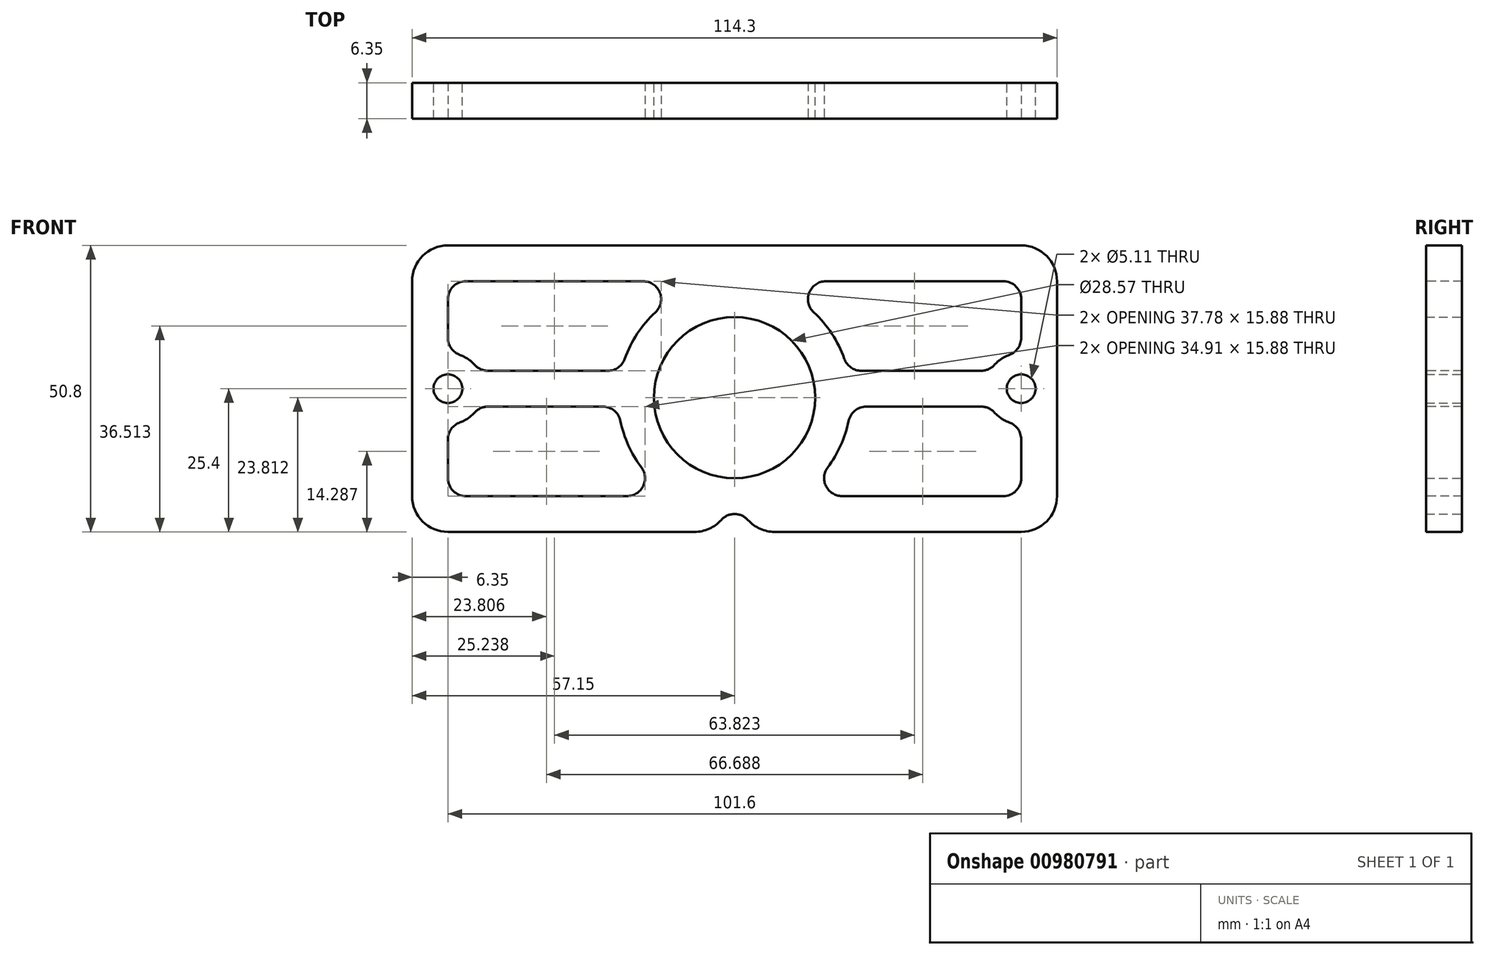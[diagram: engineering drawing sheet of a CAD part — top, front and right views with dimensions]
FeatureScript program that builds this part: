
annotation { "Feature Type Name" : "Feature", "Feature Type Description" : "" }
export const myFeature = defineFeature(function(context is Context, id is Id, definition is map)
    precondition{}
    {
        {
            var Q0;
            Q0=qCreatedBy(makeId("Front.planeOp"),FACE);
            var sketch = newSketch(context, id + "F0", { "sketchPlane" : qUnion([Q0])});
            skCircle(sketch, "E0", {"center": v(-62.07, 61.28) * mm, "radius": 32 * mm, "construction": true});
            skCircle(sketch, "E1", {"center": v(62.07, 61.28) * mm, "radius": 32 * mm, "construction": true});
            skLineSegment(sketch, "E2", {"start": v(0, 0) * mm, "end": v(0, 61.28) * mm, "construction": true});
            skLineSegment(sketch, "E3", {"start": v(-62.07, 61.28) * mm, "end": v(62.07, 61.28) * mm, "construction": true});
            skLineSegment(sketch, "E4.bottom", {"start": v(-127, 25.4) * mm, "end": v(127, 25.4) * mm, "construction": true});
            skLineSegment(sketch, "E4.top", {"start": v(-127, -25.4) * mm, "end": v(127, -25.4) * mm, "construction": true});
            skLineSegment(sketch, "E4.left", {"start": v(-127, 25.4) * mm, "end": v(-127, -25.4) * mm, "construction": true});
            skLineSegment(sketch, "E4.right", {"start": v(127, 25.4) * mm, "end": v(127, -25.4) * mm, "construction": true});
            skPoint(sketch, "E4.middle", {"position": v(0, 0) * mm});
            skCircle(sketch, "E5", {"center": v(-62.07, 61.28) * mm, "radius": 8.9 * mm, "construction": true});
            skCircle(sketch, "E6", {"center": v(62.07, 61.28) * mm, "radius": 8.9 * mm, "construction": true});
            skCircle(sketch, "E7", {"center": v(0, -1.59) * mm, "radius": 50.8 * mm, "construction": true});
            skCircle(sketch, "E8", {"center": v(-62.07, 61.28) * mm, "radius": 9.55 * mm, "construction": true});
            skCircle(sketch, "E9", {"center": v(62.07, 61.28) * mm, "radius": 9.55 * mm, "construction": true});
            skCircle(sketch, "E10", {"center": v(0, 65.72) * mm, "radius": 14.29 * mm, "construction": true});
            skCircle(sketch, "E11", {"center": v(0, -1.59) * mm, "radius": 14.29 * mm});
            skCircle(sketch, "E12", {"center": v(-114.3, 12.7) * mm, "radius": 2.55 * mm, "construction": true});
            skCircle(sketch, "E13.0.1.0", {"center": v(-114.3, -12.7) * mm, "radius": 2.55 * mm, "construction": true});
            skCircle(sketch, "E13.1.0.0", {"center": v(-88.9, 12.7) * mm, "radius": 2.55 * mm, "construction": true});
            skCircle(sketch, "E13.1.1.0", {"center": v(-88.9, -12.7) * mm, "radius": 2.55 * mm, "construction": true});
            skCircle(sketch, "E13.2.0.0", {"center": v(-63.5, 12.7) * mm, "radius": 2.55 * mm, "construction": true});
            skCircle(sketch, "E13.2.1.0", {"center": v(-63.5, -12.7) * mm, "radius": 2.55 * mm, "construction": true});
            skCircle(sketch, "E13.3.0.0", {"center": v(-38.1, 12.7) * mm, "radius": 2.55 * mm, "construction": true});
            skCircle(sketch, "E13.3.1.0", {"center": v(-38.1, -12.7) * mm, "radius": 2.55 * mm, "construction": true});
            skCircle(sketch, "E13.4.0.0", {"center": v(-12.7, 12.7) * mm, "radius": 2.55 * mm, "construction": true});
            skCircle(sketch, "E13.4.1.0", {"center": v(-12.7, -12.7) * mm, "radius": 2.55 * mm, "construction": true});
            skCircle(sketch, "E13.5.0.0", {"center": v(12.7, 12.7) * mm, "radius": 2.55 * mm, "construction": true});
            skCircle(sketch, "E13.5.1.0", {"center": v(12.7, -12.7) * mm, "radius": 2.55 * mm, "construction": true});
            skCircle(sketch, "E13.6.0.0", {"center": v(38.1, 12.7) * mm, "radius": 2.55 * mm, "construction": true});
            skCircle(sketch, "E13.6.1.0", {"center": v(38.1, -12.7) * mm, "radius": 2.55 * mm, "construction": true});
            skCircle(sketch, "E13.7.0.0", {"center": v(63.5, 12.7) * mm, "radius": 2.55 * mm, "construction": true});
            skCircle(sketch, "E13.7.1.0", {"center": v(63.5, -12.7) * mm, "radius": 2.55 * mm, "construction": true});
            skCircle(sketch, "E13.8.0.0", {"center": v(88.9, 12.7) * mm, "radius": 2.55 * mm, "construction": true});
            skCircle(sketch, "E13.8.1.0", {"center": v(88.9, -12.7) * mm, "radius": 2.55 * mm, "construction": true});
            skCircle(sketch, "E13.9.0.0", {"center": v(114.3, 12.7) * mm, "radius": 2.55 * mm, "construction": true});
            skCircle(sketch, "E13.9.1.0", {"center": v(114.3, -12.7) * mm, "radius": 2.55 * mm, "construction": true});
            skLineSegment(sketch, "E13.direction1", {"start": v(-114.3, 12.7) * mm, "end": v(-88.9, 12.7) * mm, "construction": true});
            skLineSegment(sketch, "E13.direction2", {"start": v(-114.3, 12.7) * mm, "end": v(-114.3, -12.7) * mm, "construction": true});
            skCircle(sketch, "E14", {"center": v(-50.8, 0) * mm, "radius": 2.55 * mm});
            skCircle(sketch, "E15", {"center": v(50.8, 0) * mm, "radius": 2.55 * mm});
            skCircle(sketch, "E16", {"center": v(-50.8, 0) * mm, "radius": 6.35 * mm, "construction": true});
            skCircle(sketch, "E17", {"center": v(50.8, 0) * mm, "radius": 6.35 * mm, "construction": true});
            skLineSegment(sketch, "E18", {"start": v(-74.77, 39.28) * mm, "end": v(-62.07, 61.28) * mm, "construction": true});
            skLineSegment(sketch, "E19", {"start": v(-62.07, 61.28) * mm, "end": v(-49.37, 83.27) * mm, "construction": true});
            skCircle(sketch, "E20", {"center": v(-74.77, 39.28) * mm, "radius": 2.55 * mm, "construction": true});
            skCircle(sketch, "E21", {"center": v(-49.37, 83.27) * mm, "radius": 2.55 * mm, "construction": true});
            skLineSegment(sketch, "E22.MirrorCS", {"start": v(74.77, 39.28) * mm, "end": v(62.07, 61.28) * mm, "construction": true});
            skCircle(sketch, "E23.MirrorC", {"center": v(74.77, 39.28) * mm, "radius": 2.55 * mm, "construction": true});
            skLineSegment(sketch, "E24.MirrorCS", {"start": v(62.07, 61.28) * mm, "end": v(49.37, 83.27) * mm, "construction": true});
            skCircle(sketch, "E25.MirrorC", {"center": v(49.37, 83.27) * mm, "radius": 2.55 * mm, "construction": true});
            skCircle(sketch, "E26", {"center": v(0, 65.72) * mm, "radius": 53.34 * mm, "construction": true});
            skCircle(sketch, "E27", {"center": v(0, 65.72) * mm, "radius": 25.4 * mm, "construction": true});
            skCircle(sketch, "E28", {"center": v(0, -1.59) * mm, "radius": 20.64 * mm, "construction": true});
            skCircle(sketch, "E29", {"center": v(0, 65.72) * mm, "radius": 55.88 * mm, "construction": true});
            skCircle(sketch, "E30", {"center": v(0, 91.12) * mm, "radius": 2.55 * mm, "construction": true});
            skCircle(sketch, "E31", {"center": v(0, 40.32) * mm, "radius": 2.55 * mm, "construction": true});
            skLineSegment(sketch, "E32", {"start": v(0, 40.32) * mm, "end": v(0, 65.72) * mm, "construction": true});
            skLineSegment(sketch, "E33", {"start": v(0, 65.72) * mm, "end": v(0, 91.12) * mm, "construction": true});
            skCircle(sketch, "E34", {"center": v(0, -1.59) * mm, "radius": 41.91 * mm, "construction": true});
            skCircle(sketch, "E35", {"center": v(0, -1.59) * mm, "radius": 44.45 * mm, "construction": true});
            skCircle(sketch, "E36", {"center": v(0, 65.72) * mm, "radius": 28.58 * mm, "construction": true});
            skArc(sketch, "E37", {"start": v(30.1, 62.76) * mm, "mid": v(0, 94.3) * mm, "end": v(-30.1, 62.76) * mm});
            skLineSegment(sketch, "E38.bottom", {"start": v(-57.15, 25.4) * mm, "end": v(57.15, 25.4) * mm});
            skLineSegment(sketch, "E38.top", {"start": v(-57.15, -25.4) * mm, "end": v(57.15, -25.4) * mm, "construction": true});
            skLineSegment(sketch, "E38.left", {"start": v(-57.15, 25.4) * mm, "end": v(-57.15, -25.4) * mm});
            skLineSegment(sketch, "E38.right", {"start": v(57.15, 25.4) * mm, "end": v(57.15, -25.4) * mm});
            skArc(sketch, "E39", {"start": v(3.18, -25.4) * mm, "mid": v(0, -22.22) * mm, "end": v(-3.18, -25.4) * mm});
            skLineSegment(sketch, "E40", {"start": v(-3.18, -25.4) * mm, "end": v(-57.15, -25.4) * mm});
            skLineSegment(sketch, "E41", {"start": v(3.18, -25.4) * mm, "end": v(57.15, -25.4) * mm});
            skSolve(sketch);
        }
        {
            var Q0;
            Q0=qSketchRegion(id+"F0",true);
            extrude(context, id + "F1", {"entities" : qUnion([Q0]), "depth" : 6.35 * mm, "offsetDistance" : 25.4 * mm});
        }
        {
            var Q0;
            Q0=makeQuery(id+"F1.opExtrude","SWEPT_EDGE",EDGE,{"disambiguationData":[OSD([sQuery(id+"F0.wireOp",EDGE,"E38.bottom"),sQuery(id+"F0.wireOp",EDGE,"E38.left")])]});
            var Q1;
            Q1=makeQuery(id+"F1.opExtrude","SWEPT_EDGE",EDGE,{"disambiguationData":[OSD([sQuery(id+"F0.wireOp",EDGE,"E38.top"),sQuery(id+"F0.wireOp",EDGE,"E38.left")])]});
            var Q2;
            Q2=makeQuery(id+"F1.opExtrude","SWEPT_EDGE",EDGE,{"disambiguationData":[OSD([sQuery(id+"F0.wireOp",EDGE,"E38.top"),sQuery(id+"F0.wireOp",EDGE,"E38.right")])]});
            var Q3;
            Q3=makeQuery(id+"F1.opExtrude","SWEPT_EDGE",EDGE,{"disambiguationData":[OSD([sQuery(id+"F0.wireOp",EDGE,"E38.bottom"),sQuery(id+"F0.wireOp",EDGE,"E38.right")])]});
            var Q4;
            Q4=makeQuery(id+"F1.opExtrude","SWEPT_EDGE",EDGE,{"disambiguationData":[OSD([sQuery(id+"F0.wireOp",EDGE,"E39"),sQuery(id+"F0.wireOp",EDGE,"E40")])]});
            var Q5;
            Q5=makeQuery(id+"F1.opExtrude","SWEPT_EDGE",EDGE,{"disambiguationData":[OSD([sQuery(id+"F0.wireOp",EDGE,"E39"),sQuery(id+"F0.wireOp",EDGE,"E41")])]});
            fillet(context, id + "F2", {"entities" : qUnion([Q0, Q1, Q2, Q3, Q4, Q5]), "radius" : 6.35 * mm, "tangentPropagation" : true, "allowEdgeOverflow" : false});
        }
        {
            var Q0;
            Q0=makeQuery(id+"F1.opExtrude","CAP_FACE",FACE,{"disambiguationData":[OSD([sQuery(id+"F0.wireOp",EDGE,"E11"),sQuery(id+"F0.wireOp",EDGE,"E14"),sQuery(id+"F0.wireOp",EDGE,"E15"),sQuery(id+"F0.wireOp",EDGE,"E38.bottom"),sQuery(id+"F0.wireOp",EDGE,"E38.left"),sQuery(id+"F0.wireOp",EDGE,"E38.right"),sQuery(id+"F0.wireOp",EDGE,"E39"),sQuery(id+"F0.wireOp",EDGE,"E40"),sQuery(id+"F0.wireOp",EDGE,"E41")])],"isStart":false});
            var sketch = newSketch(context, id + "F3", { "sketchPlane" : qUnion([Q0])});
            skLineSegment(sketch, "E42.0", {"start": v(-50.8, 19.05) * mm, "end": v(-50.8, -19.05) * mm, "construction": true});
            skLineSegment(sketch, "E42.1", {"start": v(50.8, 19.05) * mm, "end": v(50.8, -19.05) * mm, "construction": true});
            skLineSegment(sketch, "E42.2", {"start": v(7.1, -19.05) * mm, "end": v(50.8, -19.05) * mm, "construction": true});
            skLineSegment(sketch, "E42.3", {"start": v(-50.8, 19.05) * mm, "end": v(50.8, 19.05) * mm, "construction": true});
            skArc(sketch, "E42.4", {"start": v(7.1, -19.05) * mm, "mid": v(0, -15.88) * mm, "end": v(-7.1, -19.05) * mm, "construction": true});
            skLineSegment(sketch, "E42.5", {"start": v(-7.1, -19.05) * mm, "end": v(-50.8, -19.05) * mm, "construction": true});
            skCircle(sketch, "E43", {"center": v(-50.8, 0) * mm, "radius": 6.35 * mm, "construction": true});
            skCircle(sketch, "E44", {"center": v(0, -1.59) * mm, "radius": 20.64 * mm, "construction": true});
            skCircle(sketch, "E45", {"center": v(50.8, 0) * mm, "radius": 6.35 * mm, "construction": true});
            skLineSegment(sketch, "E46", {"start": v(-43.7, 3.18) * mm, "end": v(-22.45, 3.18) * mm});
            skLineSegment(sketch, "E47", {"start": v(-43.7, -3.18) * mm, "end": v(-23.33, -3.18) * mm});
            skLineSegment(sketch, "E48", {"start": v(-50.8, 8.98) * mm, "end": v(-50.8, 15.87) * mm});
            skLineSegment(sketch, "E49", {"start": v(-47.63, 19.05) * mm, "end": v(-16.19, 19.05) * mm});
            skArc(sketch, "E50", {"start": v(-46.07, 4.23) * mm, "mid": v(-47.26, 5.27) * mm, "end": v(-48.68, 5.99) * mm});
            skArc(sketch, "E51", {"start": v(-14.03, 13.55) * mm, "mid": v(-17.25, 9.75) * mm, "end": v(-19.46, 5.3) * mm});
            skPoint(sketch, "E52.visualSharp", {"position": v(-50.8, 19.05) * mm});
            skArc(sketch, "E52.filletArc", {"start": v(-47.63, 19.05) * mm, "mid": v(-49.87, 18.12) * mm, "end": v(-50.8, 15.87) * mm});
            skPoint(sketch, "E53.visualSharp", {"position": v(-50.8, 6.35) * mm});
            skArc(sketch, "E53.filletArc", {"start": v(-50.8, 8.98) * mm, "mid": v(-50.22, 7.15) * mm, "end": v(-48.68, 5.99) * mm});
            skPoint(sketch, "E54.visualSharp", {"position": v(-45.3, 3.18) * mm});
            skArc(sketch, "E54.filletArc", {"start": v(-46.07, 4.23) * mm, "mid": v(-45, 3.45) * mm, "end": v(-43.7, 3.18) * mm});
            skPoint(sketch, "E55.visualSharp", {"position": v(-20.08, 3.17) * mm});
            skArc(sketch, "E55.filletArc", {"start": v(-22.45, 3.18) * mm, "mid": v(-20.62, 3.76) * mm, "end": v(-19.46, 5.3) * mm});
            skPoint(sketch, "E56.visualSharp", {"position": v(0, 19.05) * mm});
            skArc(sketch, "E56.filletArc", {"start": v(-14.03, 13.55) * mm, "mid": v(-13.23, 17.03) * mm, "end": v(-16.19, 19.05) * mm});
            skLineSegment(sketch, "E57", {"start": v(-50.8, 0) * mm, "end": v(50.8, 0) * mm, "construction": true});
            skLineSegment(sketch, "E58", {"start": v(0, -25.4) * mm, "end": v(0, 19.05) * mm, "construction": true});
            skArc(sketch, "E59.MirrorCS", {"start": v(46.07, 4.23) * mm, "mid": v(47.26, 5.27) * mm, "end": v(48.68, 5.99) * mm});
            skArc(sketch, "E60.MirrorCS", {"start": v(46.07, 4.23) * mm, "mid": v(45, 3.45) * mm, "end": v(43.7, 3.18) * mm});
            skArc(sketch, "E61.MirrorCS", {"start": v(50.8, 8.98) * mm, "mid": v(50.22, 7.15) * mm, "end": v(48.68, 5.99) * mm});
            skArc(sketch, "E62.MirrorCS", {"start": v(47.63, 19.05) * mm, "mid": v(49.87, 18.12) * mm, "end": v(50.8, 15.87) * mm});
            skArc(sketch, "E63.MirrorCS", {"start": v(22.45, 3.18) * mm, "mid": v(20.62, 3.76) * mm, "end": v(19.46, 5.3) * mm});
            skArc(sketch, "E64.MirrorCS", {"start": v(14.03, 13.55) * mm, "mid": v(13.23, 17.03) * mm, "end": v(16.19, 19.05) * mm});
            skPoint(sketch, "E65.MirrorP", {"position": v(50.8, 19.05) * mm});
            skArc(sketch, "E66.MirrorCS", {"start": v(14.03, 13.55) * mm, "mid": v(17.25, 9.75) * mm, "end": v(19.46, 5.3) * mm});
            skPoint(sketch, "E67.MirrorP", {"position": v(50.8, 6.35) * mm});
            skLineSegment(sketch, "E68.MirrorCS", {"start": v(43.7, 3.18) * mm, "end": v(22.45, 3.18) * mm});
            skLineSegment(sketch, "E69.MirrorCS", {"start": v(50.8, 8.98) * mm, "end": v(50.8, 15.87) * mm});
            skPoint(sketch, "E70.MirrorP", {"position": v(45.3, 3.18) * mm});
            skLineSegment(sketch, "E71.MirrorCS", {"start": v(47.63, 19.05) * mm, "end": v(16.19, 19.05) * mm});
            skPoint(sketch, "E72.MirrorP", {"position": v(20.08, 3.17) * mm});
            skLineSegment(sketch, "E73", {"start": v(-50.8, -8.98) * mm, "end": v(-50.8, -15.88) * mm});
            skLineSegment(sketch, "E74", {"start": v(-47.63, -19.05) * mm, "end": v(-19.05, -19.05) * mm});
            skArc(sketch, "E75", {"start": v(-20.22, -5.71) * mm, "mid": v(-18.82, -10.05) * mm, "end": v(-16.5, -13.97) * mm});
            skArc(sketch, "E76", {"start": v(-48.68, -5.99) * mm, "mid": v(-47.26, -5.27) * mm, "end": v(-46.07, -4.23) * mm});
            skPoint(sketch, "E77.visualSharp", {"position": v(-50.8, -6.35) * mm});
            skArc(sketch, "E77.filletArc", {"start": v(-48.68, -5.99) * mm, "mid": v(-50.22, -7.15) * mm, "end": v(-50.8, -8.98) * mm});
            skPoint(sketch, "E78.visualSharp", {"position": v(-45.3, -3.18) * mm});
            skArc(sketch, "E78.filletArc", {"start": v(-43.7, -3.17) * mm, "mid": v(-45, -3.45) * mm, "end": v(-46.07, -4.23) * mm});
            skPoint(sketch, "E79.visualSharp", {"position": v(-20.58, -3.18) * mm});
            skArc(sketch, "E79.filletArc", {"start": v(-20.22, -5.71) * mm, "mid": v(-21.32, -3.9) * mm, "end": v(-23.33, -3.18) * mm});
            skPoint(sketch, "E80.visualSharp", {"position": v(-11, -19.05) * mm});
            skArc(sketch, "E80.filletArc", {"start": v(-19.05, -19.05) * mm, "mid": v(-16.21, -17.3) * mm, "end": v(-16.5, -13.97) * mm});
            skPoint(sketch, "E81.visualSharp", {"position": v(-50.8, -19.05) * mm});
            skArc(sketch, "E81.filletArc", {"start": v(-50.8, -15.88) * mm, "mid": v(-49.87, -18.12) * mm, "end": v(-47.63, -19.05) * mm});
            skArc(sketch, "E82.MirrorCS", {"start": v(48.68, -5.99) * mm, "mid": v(50.22, -7.15) * mm, "end": v(50.8, -8.98) * mm});
            skArc(sketch, "E83.MirrorCS", {"start": v(43.7, -3.17) * mm, "mid": v(45, -3.45) * mm, "end": v(46.07, -4.23) * mm});
            skArc(sketch, "E84.MirrorCS", {"start": v(20.22, -5.71) * mm, "mid": v(21.32, -3.9) * mm, "end": v(23.33, -3.18) * mm});
            skPoint(sketch, "E85.MirrorP", {"position": v(20.58, -3.18) * mm});
            skArc(sketch, "E86.MirrorCS", {"start": v(48.68, -5.99) * mm, "mid": v(47.26, -5.27) * mm, "end": v(46.07, -4.23) * mm});
            skArc(sketch, "E87.MirrorCS", {"start": v(19.05, -19.05) * mm, "mid": v(16.21, -17.3) * mm, "end": v(16.5, -13.97) * mm});
            skLineSegment(sketch, "E88.MirrorCS", {"start": v(43.7, -3.18) * mm, "end": v(23.33, -3.18) * mm});
            skLineSegment(sketch, "E89.MirrorCS", {"start": v(50.8, -8.98) * mm, "end": v(50.8, -15.88) * mm});
            skPoint(sketch, "E90.MirrorP", {"position": v(50.8, -19.05) * mm});
            skLineSegment(sketch, "E91.MirrorCS", {"start": v(47.63, -19.05) * mm, "end": v(19.05, -19.05) * mm});
            skPoint(sketch, "E92.MirrorP", {"position": v(50.8, -6.35) * mm});
            skArc(sketch, "E93.MirrorCS", {"start": v(50.8, -15.88) * mm, "mid": v(49.87, -18.12) * mm, "end": v(47.63, -19.05) * mm});
            skPoint(sketch, "E94.MirrorP", {"position": v(11, -19.05) * mm});
            skPoint(sketch, "E95.MirrorP", {"position": v(45.3, -3.18) * mm});
            skArc(sketch, "E96.MirrorCS", {"start": v(20.22, -5.71) * mm, "mid": v(18.82, -10.05) * mm, "end": v(16.5, -13.97) * mm});
            skSolve(sketch);
        }
        {
            var Q0;
            Q0 = qSketchRegion(id + "F3", true);
            extrude(context, id + "F4", {"entities" : qUnion([Q0]), "operationType" : NewBodyOperationType.REMOVE, "oppositeDirection" : true, "depth" : 25.4 * mm, "offsetDistance" : 25.4 * mm});
        }
    });
